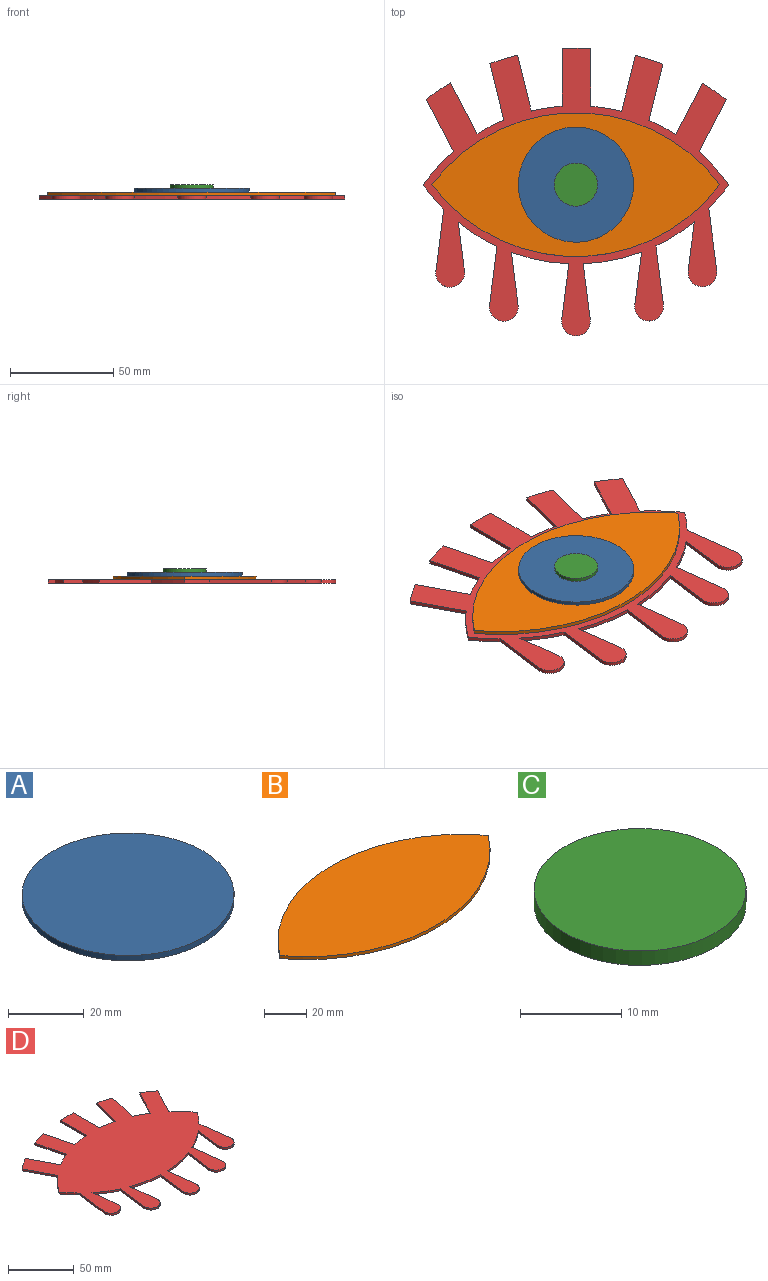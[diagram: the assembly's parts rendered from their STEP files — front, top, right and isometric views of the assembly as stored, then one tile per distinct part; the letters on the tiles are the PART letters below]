
ASSEMBLY  parts=4 mates=3
PART A: 3 faces, bbox 55.9x55.9x1.7 mm
  f0: cylinder r=27.94mm len=55.88mm, axis (0,0,-1), area 306.6mm2, adj f1,f2
  f1: plane 55.88x55.88mm, normal (0,0,1), area 2452.5mm2, adj f0
  f2: plane 55.88x55.88mm, normal (0,0,-1), area 2452.5mm2, adj f0
PART B: 4 faces, bbox 139.7x69.9x1.7 mm
  f0: cylinder r=87.31mm len=139.7mm, axis (0,0,-1), area 282.8mm2, adj f1,f2,f3
  f1: cylinder r=87.31mm len=139.7mm, axis (0,0,-1), area 282.8mm2, adj f0,f2,f3
  f2: plane 139.7x69.85mm, normal (0,0,1), area 6819.9mm2, adj f0,f1
  f3: plane 139.7x69.85mm, normal (0,0,-1), area 6819.9mm2, adj f0,f1
PART C: 3 faces, bbox 21x21x1.7 mm
  f0: cylinder r=10.48mm len=20.96mm, axis (0,0,-1), area 115mm2, adj f1,f2
  f1: plane 20.96x20.96mm, normal (0,0,1), area 344.9mm2, adj f0
  f2: plane 20.96x20.96mm, normal (0,0,-1), area 344.9mm2, adj f0
PART D: 44 faces, bbox 148.3x139.7x1.7 mm
  f0: cylinder r=90.8mm len=28.34mm, axis (0,0,-1), area 50.7mm2, adj f27,f28,f35,f41
  f1: cylinder r=90.8mm len=11.55mm, axis (0,0,-1), area 26.3mm2, adj f22,f27,f28,f39
  f2: cylinder r=90.8mm len=18.64mm, axis (0,0,-1), area 38.6mm2, adj f27,f28,f36,f38
  f3: cylinder r=90.8mm len=27.89mm, axis (0,0,-1), area 49.9mm2, adj f27,f28,f32,f42
  f4: cylinder r=90.8mm len=18.79mm, axis (0,0,-1), area 38.8mm2, adj f27,f28,f29,f33
  f5: plane 27.39x6.75mm, normal (0.97,-0.24,0), area 49.3mm2, adj f6,f26,f27,f28
  f6: cylinder r=118.75mm len=13.36mm, axis (0,0,-1), area 24.5mm2, adj f5,f7,f27,f28
  f7: plane 27.13x6.69mm, normal (-0.97,0.24,0), area 48.8mm2, adj f6,f8,f27,f28
  f8: cylinder r=90.8mm len=14.91mm, axis (0,0,-1), area 26.4mm2, adj f7,f9,f27,f28
  f9: plane 28.01x1.75mm, normal (1,0,0), area 48.9mm2, adj f8,f10,f27,f28
  f10: cylinder r=118.75mm len=13.97mm, axis (0,0,-1), area 24.4mm2, adj f9,f11,f27,f28
  f11: plane 28x1.75mm, normal (-1,0,0), area 48.9mm2, adj f10,f12,f27,f28
  f12: cylinder r=90.8mm len=14.94mm, axis (0,0,-1), area 26.4mm2, adj f11,f13,f27,f28
  f13: plane 27.13x6.69mm, normal (0.97,0.24,0), area 48.8mm2, adj f12,f14,f27,f28
  f14: cylinder r=118.75mm len=13.37mm, axis (0,0,-1), area 24.5mm2, adj f13,f15,f27,f28
  f15: plane 27.38x6.75mm, normal (-0.97,-0.24,0), area 49.2mm2, adj f14,f16,f27,f28
  f16: cylinder r=90.8mm len=13.04mm, axis (0,0,-1), area 25.7mm2, adj f15,f17,f27,f28
  f17: plane 24.79x13.01mm, normal (0.89,0.46,0), area 48.9mm2, adj f16,f18,f27,f28
  f18: cylinder r=118.75mm len=11.61mm, axis (0,0,-1), area 24.6mm2, adj f17,f19,f27,f28
  f19: plane 25.25x13.25mm, normal (-0.89,-0.46,0), area 49.8mm2, adj f18,f20,f27,f28
  f20: cylinder r=90.8mm len=16.27mm, axis (0,0,-1), area 38.4mm2, adj f19,f21,f27,f28
  f21: cylinder r=90.8mm len=11.84mm, axis (0,0,-1), area 27.1mm2, adj f20,f27,f28,f30
  f22: cylinder r=90.8mm len=16.01mm, axis (0,0,-1), area 37.7mm2, adj f1,f23,f27,f28
  f23: plane 25.27x13.26mm, normal (0.89,-0.46,0), area 49.8mm2, adj f22,f24,f27,f28
  f24: cylinder r=118.75mm len=11.59mm, axis (0,0,-1), area 24.6mm2, adj f23,f25,f27,f28
  f25: plane 24.8x13.02mm, normal (-0.89,0.46,0), area 48.9mm2, adj f24,f26,f27,f28
  f26: cylinder r=90.8mm len=12.98mm, axis (0,0,-1), area 25.6mm2, adj f5,f25,f27,f28
  f27: plane 148.34x139.7mm, normal (0,0,1), area 11806.7mm2, adj f0,f1,f2,f3,f4,f5,f6,f7
  f28: plane 148.34x139.7mm, normal (0,0,-1), area 11806.7mm2, adj f0,f1,f2,f3,f4,f5,f6,f7
  f29: plane 23.7x3.01mm, normal (0.99,0.13,0), area 41.7mm2, adj f4,f27,f28,f31
  f30: plane 30.24x3.84mm, normal (-0.99,0.13,0), area 53.2mm2, adj f21,f27,f28,f31
  f31: cylinder r=6.99mm len=13.97mm, axis (0,0,1), area 41mm2, adj f27,f28,f29,f30
  f32: plane 25.61x3.28mm, normal (0.99,0.13,0), area 45.1mm2, adj f3,f27,f28,f34
  f33: plane 28.53x3.6mm, normal (-0.99,0.13,0), area 50.2mm2, adj f4,f27,f28,f34
  f34: cylinder r=6.99mm len=13.97mm, axis (0,0,1), area 41.4mm2, adj f27,f28,f32,f33
  f35: plane 25.59x3.26mm, normal (-0.99,0.13,0), area 45mm2, adj f0,f27,f28,f37
  f36: plane 28.54x3.61mm, normal (0.99,0.13,0), area 50.2mm2, adj f2,f27,f28,f37
  f37: cylinder r=6.99mm len=13.97mm, axis (0,0,1), area 41.4mm2, adj f27,f28,f35,f36
  f38: plane 23.66x3.02mm, normal (-0.99,0.13,0), area 41.6mm2, adj f2,f27,f28,f40
  f39: plane 30.05x3.8mm, normal (0.99,0.13,0), area 52.9mm2, adj f1,f27,f28,f40
  f40: cylinder r=6.99mm len=13.97mm, axis (0,0,1), area 41.4mm2, adj f27,f28,f38,f39
  f41: plane 27.13x3.45mm, normal (0.99,0.13,0), area 47.8mm2, adj f0,f27,f28,f43
  f42: plane 27.13x3.45mm, normal (-0.99,0.13,0), area 47.8mm2, adj f3,f27,f28,f43
  f43: cylinder r=6.99mm len=13.97mm, axis (0,0,1), area 41.4mm2, adj f27,f28,f41,f42
PLACE A t=(-2.8,-13.94,-10.11)mm
PLACE B t=(-2.59,-13.94,-10.11)mm
PLACE C t=(-2.8,-13.94,-11.7)mm
PLACE D t=(-2.52,-14.01,-10.11)mm
MATE planar B.f3 <-> D.f27  axis (0,0,-1) through (-2.59,-13.94,-8.37)mm
MATE fastened C.f0 <-> A.f0  axis (0,0,-1) through (-2.59,-13.94,-4.88)mm
MATE fastened A.f0 <-> B.f2  axis (0,0,-1) through (-2.59,-13.94,-6.62)mm
